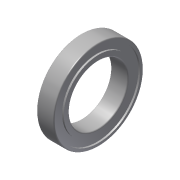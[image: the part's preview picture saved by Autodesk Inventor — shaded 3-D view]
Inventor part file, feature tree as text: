
AUTODESK INVENTOR PART (.ipt)
format: ipt  version: 2013 (Build 170138000, 138)  size: 158,208 bytes
history: native  units: in
note: dims shown in document units (in); Inventor stores cm internally (conversion verified against a paired STEP export)
features: fillet x1, imported_body x1
ambient origin geometry x8: Origin, YZ Plane, XZ Plane, XY Plane, X Axis, Y Axis, Z Axis, Center Point
feature tree (2):
  fillet  "Fillet1"  [1 undecoded]
  imported_body  "Base1"
note: 1 required parameter value undecoded (feature->parameter linkage not recoverable at this tier; creation-order binding heuristic only, values carry confidence <= 0.55)
